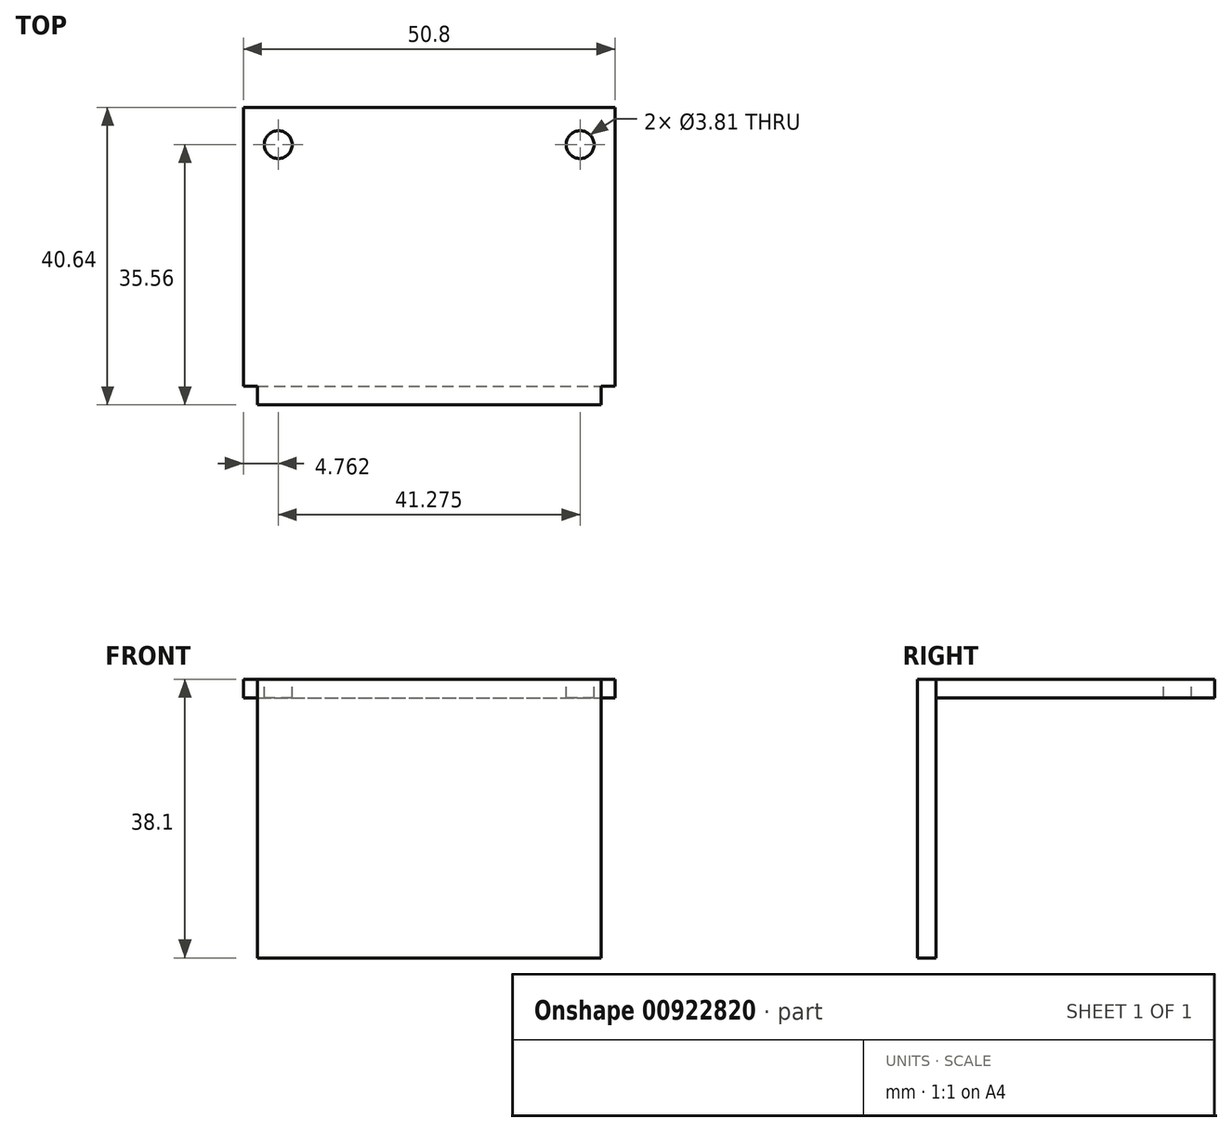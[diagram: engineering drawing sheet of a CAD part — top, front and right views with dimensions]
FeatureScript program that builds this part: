
annotation { "Feature Type Name" : "Feature", "Feature Type Description" : "" }
export const myFeature = defineFeature(function(context is Context, id is Id, definition is map)
    precondition{}
    {
        {
            var Q0;
            Q0=qCreatedBy(makeId("Top.planeOp"),FACE);
            var sketch = newSketch(context, id + "F0", { "sketchPlane" : qUnion([Q0])});
            skLineSegment(sketch, "E0.bottom", {"start": v(-25.4, 19.05) * mm, "end": v(25.4, 19.05) * mm});
            skLineSegment(sketch, "E0.top", {"start": v(-25.4, -19.05) * mm, "end": v(25.4, -19.05) * mm});
            skLineSegment(sketch, "E0.left", {"start": v(-25.4, 19.05) * mm, "end": v(-25.4, -19.05) * mm});
            skLineSegment(sketch, "E0.right", {"start": v(25.4, 19.05) * mm, "end": v(25.4, -19.05) * mm});
            skPoint(sketch, "E0.middle", {"position": v(0, 0) * mm});
            skSolve(sketch);
        }
        {
            var Q0;
            Q0 = qSketchRegion(id + "F0", true);
            extrude(context, id + "F1", {"entities" : qUnion([Q0]), "depth" : 2.54 * mm, "offsetDistance" : 25.4 * mm});
        }
        {
            var Q0;
            Q0=makeQuery(id+"F1.opExtrude","SWEPT_FACE",FACE,{"disambiguationData":[OSD([sQuery(id+"F0.wireOp",EDGE,"E0.top")])]});
            var sketch = newSketch(context, id + "F2", { "sketchPlane" : qUnion([Q0])});
            skLineSegment(sketch, "E1.bottom", {"start": v(-23.5, 2.54) * mm, "end": v(23.5, 2.54) * mm});
            skLineSegment(sketch, "E1.top", {"start": v(-23.5, -35.56) * mm, "end": v(23.5, -35.56) * mm});
            skLineSegment(sketch, "E1.left", {"start": v(-23.5, 2.54) * mm, "end": v(-23.5, -35.56) * mm});
            skLineSegment(sketch, "E1.right", {"start": v(23.5, 2.54) * mm, "end": v(23.5, -35.56) * mm});
            skSolve(sketch);
        }
        {
            var Q0;
            Q0 = qSketchRegion(id + "F2", true);
            extrude(context, id + "F3", {"entities" : qUnion([Q0]), "operationType" : NewBodyOperationType.ADD, "depth" : 2.54 * mm, "offsetDistance" : 25.4 * mm});
        }
        {
            var Q0;
            Q0=makeQuery(id+"F3.boolean.opBoolean","MERGE",FACE,{"derivedFrom":[makeQuery(id+"F1.opExtrude","CAP_FACE",FACE,{"disambiguationData":[OSD([sQuery(id+"F0.wireOp",EDGE,"E0.bottom"),sQuery(id+"F0.wireOp",EDGE,"E0.top"),sQuery(id+"F0.wireOp",EDGE,"E0.left"),sQuery(id+"F0.wireOp",EDGE,"E0.right")])],"isStart":false}),makeQuery(id+"F3.opExtrude","SWEPT_FACE",FACE,{"disambiguationData":[OSD([sQuery(id+"F2.wireOp",EDGE,"cdHErLTB-BIyk-onr7-rtOh-9mPCrM14wL8Y.bottom")])]})]});
            var sketch = newSketch(context, id + "F4", { "sketchPlane" : qUnion([Q0])});
            skCircle(sketch, "E2", {"center": v(20.64, 13.97) * mm, "radius": 1.9 * mm});
            skCircle(sketch, "E3", {"center": v(-20.64, 13.97) * mm, "radius": 1.9 * mm});
            skSolve(sketch);
        }
        {
            var Q0;
            Q0 = qSketchRegion(id + "F4", true);
            extrude(context, id + "F5", {"entities" : qUnion([Q0]), "operationType" : NewBodyOperationType.REMOVE, "endBound" : BoundingType.THROUGH_ALL, "oppositeDirection" : true, "depth" : 25.4 * mm, "offsetDistance" : 25.4 * mm});
        }
    });
